# Revit family: JOMA_P1 & P2
name_source: partatom
category: Structural Connections
revit_build: Autodesk Revit Structure 2012 (Build: 20110309_2315(x64)
units: mm (PartAtom-declared; Revit-internal decimal feet)

## types (4) — shared parameters
Länk Joma Dimensioneringsverktyg = http://www.joma.se
Material = Varmförzinkad stålplåt
b = 60 mm  [stored 0.19685 ft]
h = 90 mm  [stored 0.295276 ft]
l = 60 mm  [stored 0.19685 ft]
t = 2.5 mm  [stored 0.0082021 ft]
zero-valued in all types: Default Elevation

## per-type parameters (varying)
| type | Dim. för bultinfästning | Dim. för spikhål | Typ | Vikt | Vinkelbeslag P1 | Vinkelbeslag P2 |
| 4210012 | 12 mm  [stored 0.0393701 ft] | 6 mm  [stored 0.019685 ft] | VINKEL P1 4210012 | 0,156 | Yes | No |
| 4210010 | 10.2 mm  [stored 0.0334646 ft] | 5.1 mm  [stored 0.0167323 ft] | VINKEL P1 4210010 | 0,158 | Yes | No |
| 4220010 | 10.2 mm  [stored 0.0334646 ft] | 5.1 mm  [stored 0.0167323 ft] | VINKEL P2 4220010 | 0,154 | No | Yes |
| 4220012 | 12 mm  [stored 0.0393701 ft] | 6 mm  [stored 0.019685 ft] | VINKEL P2 4220012 | 0,154 | No | Yes |

note: [stored X ft] marks values corroborated as IEEE doubles in the binary element streams (Revit-internal decimal feet)

## geometry (parser evidence)
native form markers: Sweep x2
no freeform markers — native parametric forms only
